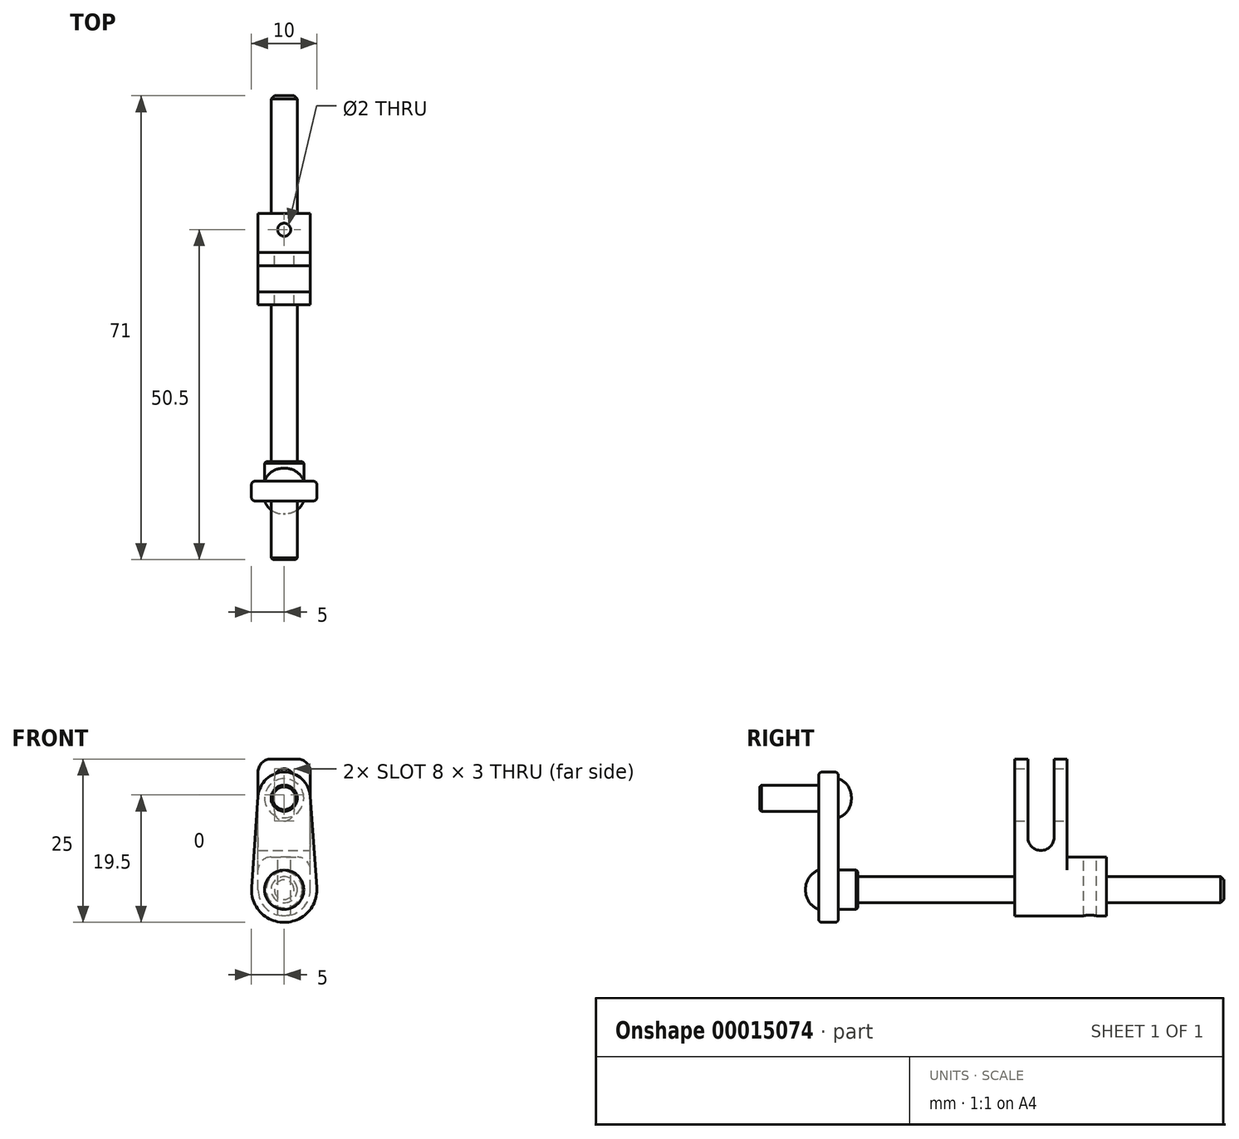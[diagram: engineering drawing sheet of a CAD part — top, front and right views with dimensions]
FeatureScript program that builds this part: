
annotation { "Feature Type Name" : "Feature", "Feature Type Description" : "" }
export const myFeature = defineFeature(function(context is Context, id is Id, definition is map)
    precondition{}
    {
        {
            var Q0;
            Q0=qCreatedBy(makeId("Front.planeOp"),FACE);
            var sketch = newSketch(context, id + "F0", { "sketchPlane" : qUnion([Q0])});
            skCircle(sketch, "E0", {"center": v(0, 0) * mm, "radius": 2 * mm});
            skArc(sketch, "E1", {"start": v(-4.99, 0.36) * mm, "mid": v(0, -5) * mm, "end": v(4.99, 0.36) * mm});
            skCircle(sketch, "E2", {"center": v(0, 14) * mm, "radius": 2 * mm});
            skArc(sketch, "E3", {"start": v(3.99, 14.29) * mm, "mid": v(0, 18) * mm, "end": v(-3.99, 14.29) * mm});
            skLineSegment(sketch, "E4", {"start": v(0, 0) * mm, "end": v(0, 19.62) * mm, "construction": true});
            skLineSegment(sketch, "E5", {"start": v(-3.99, 14.29) * mm, "end": v(-4.99, 0.36) * mm});
            skLineSegment(sketch, "E6", {"start": v(4.99, 0.36) * mm, "end": v(3.99, 14.29) * mm});
            skSolve(sketch);
        }
        {
            var Q0;
            Q0=makeQuery(id+"F0.imprint","IMPRINT",FACE,{"disambiguationData":[TD([[makeQuery(id+"F0.imprint","IMPRINT",EDGE,{"derivedFrom":sQuery(id+"F0.wireOp",EDGE,"E0")}),-1.0]])]});
            extrude(context, id + "F1", {"entities" : qUnion([Q0]), "endBound" : BoundingType.SYMMETRIC, "depth" : 3 * mm});
        }
        {
            var Q0;
            Q0=makeQuery(id+"F1.opExtrude","CAP_EDGE",EDGE,{"disambiguationData":[OSD([sQuery(id+"F0.wireOp",EDGE,"E6")])],"isStart":false});
            var Q1;
            Q1=makeQuery(id+"F1.opExtrude","CAP_EDGE",EDGE,{"disambiguationData":[OSD([sQuery(id+"F0.wireOp",EDGE,"E6")])],"isStart":true});
            fillet(context, id + "F2", {"entities" : qUnion([Q0, Q1]), "radius" : .5 * mm, "tangentPropagation" : true, "allowEdgeOverflow" : false});
        }
        {
            var Q0;
            Q0=makeQuery(id+"F1.opExtrude","CAP_FACE",FACE,{"disambiguationData":[OSD([sQuery(id+"F0.wireOp",EDGE,"E0"),sQuery(id+"F0.wireOp",EDGE,"E1"),sQuery(id+"F0.wireOp",EDGE,"E2"),sQuery(id+"F0.wireOp",EDGE,"E3"),sQuery(id+"F0.wireOp",EDGE,"E5"),sQuery(id+"F0.wireOp",EDGE,"E6")])],"isStart":true});
            var sketch = newSketch(context, id + "F3", { "sketchPlane" : qUnion([Q0])});
            skCircle(sketch, "E7.0", {"center": v(0, 14) * mm, "radius": 2 * mm});
            skSolve(sketch);
        }
        {
            var Q0;
            Q0=makeQuery(id+"F3.imprint","IMPRINT",FACE,{"disambiguationData":[TD([[makeQuery(id+"F3.imprint","IMPRINT",EDGE,{"derivedFrom":sQuery(id+"F3.wireOp",EDGE,"E7.0")}),-1.0]])]});
            extrude(context, id + "F4", {"entities" : qUnion([Q0]), "oppositeDirection" : true, "depth" : 12 * mm});
        }
        {
            var Q0;
            Q0=makeQuery(id+"F4.opExtrude","CAP_FACE",FACE,{"disambiguationData":[OSD([sQuery(id+"F3.wireOp",EDGE,"E7.0")])],"isStart":true});
            var sketch = newSketch(context, id + "F5", { "sketchPlane" : qUnion([Q0])});
            skCircle(sketch, "E8.0.0", {"center": v(0, 14) * mm, "radius": 2 * mm});
            skCircle(sketch, "E9", {"center": v(0, 14) * mm, "radius": 3 * mm});
            skSolve(sketch);
        }
        {
            var Q0;
            Q0=makeQuery(id+"F5.imprint","IMPRINT",FACE,{"disambiguationData":[TD([[makeQuery(id+"F5.imprint","IMPRINT",EDGE,{"derivedFrom":sQuery(id+"F5.wireOp",EDGE,"E8.0.0")}),1.0]])]});
            var Q1;
            Q1=makeQuery(id+"F5.imprint","IMPRINT",FACE,{"disambiguationData":[TD([[makeQuery(id+"F5.imprint","IMPRINT",EDGE,{"derivedFrom":sQuery(id+"F5.wireOp",EDGE,"E8.0.0")}),-1.0]])]});
            extrude(context, id + "F6", {"entities" : qUnion([Q0, Q1]), "operationType" : NewBodyOperationType.ADD, "depth" : 2 * mm});
        }
        {
            var Q0;
            Q0=makeQuery(id+"F6.opExtrude","CAP_EDGE",EDGE,{"disambiguationData":[OSD([sQuery(id+"F5.wireOp",EDGE,"E9")])],"isStart":false});
            fillet(context, id + "F7", {"entities" : qUnion([Q0]), "radius" : 3 * mm, "tangentPropagation" : true, "allowEdgeOverflow" : false});
        }
        {
            var Q0;
            Q0=makeQuery(id+"F4.opExtrude","CAP_EDGE",EDGE,{"disambiguationData":[OSD([sQuery(id+"F3.wireOp",EDGE,"E7.0")])],"isStart":false});
            chamfer(context, id + "F8", {"entities" : qUnion([Q0]), "width" : .25 * mm, "tangentPropagation" : true});
        }
        {
            var Q0;
            Q0=makeQuery(id+"F1.opExtrude","CAP_FACE",FACE,{"disambiguationData":[OSD([sQuery(id+"F0.wireOp",EDGE,"E0"),sQuery(id+"F0.wireOp",EDGE,"E1"),sQuery(id+"F0.wireOp",EDGE,"E2"),sQuery(id+"F0.wireOp",EDGE,"E3"),sQuery(id+"F0.wireOp",EDGE,"E5"),sQuery(id+"F0.wireOp",EDGE,"E6")])],"isStart":true});
            var sketch = newSketch(context, id + "F9", { "sketchPlane" : qUnion([Q0])});
            skCircle(sketch, "E10.0", {"center": v(0, 0) * mm, "radius": 2 * mm});
            skCircle(sketch, "E11", {"center": v(0, 0) * mm, "radius": 3 * mm});
            skSolve(sketch);
        }
        {
            var Q0;
            Q0=makeQuery(id+"F9.imprint","IMPRINT",FACE,{"disambiguationData":[TD([[makeQuery(id+"F9.imprint","IMPRINT",EDGE,{"derivedFrom":sQuery(id+"F9.wireOp",EDGE,"E10.0")}),-1.0]])]});
            var Q1;
            Q1=makeQuery(id+"F1.opExtrude","CAP_FACE",FACE,{"disambiguationData":[OSD([sQuery(id+"F0.wireOp",EDGE,"E0"),sQuery(id+"F0.wireOp",EDGE,"E1"),sQuery(id+"F0.wireOp",EDGE,"E2"),sQuery(id+"F0.wireOp",EDGE,"E3"),sQuery(id+"F0.wireOp",EDGE,"E5"),sQuery(id+"F0.wireOp",EDGE,"E6")])],"isStart":false});
            extrude(context, id + "F10", {"entities" : qUnion([Q0]), "endBound" : BoundingType.UP_TO_SURFACE, "oppositeDirection" : true, "endBoundEntityFace" : qUnion([Q1]), "depth" : 25 * mm});
        }
        {
            var Q0;
            Q0=makeQuery(id+"F10.opExtrude","CAP_FACE",FACE,{"disambiguationData":[OSD([sQuery(id+"F9.wireOp",EDGE,"E10.0")])],"isStart":false});
            var sketch = newSketch(context, id + "F11", { "sketchPlane" : qUnion([Q0])});
            skCircle(sketch, "E12.0", {"center": v(0, 0) * mm, "radius": 2 * mm});
            skCircle(sketch, "E13", {"center": v(0, 0) * mm, "radius": 3 * mm});
            skSolve(sketch);
        }
        {
            var Q0;
            Q0=makeQuery(id+"F11.imprint","IMPRINT",FACE,{"disambiguationData":[TD([[makeQuery(id+"F11.imprint","IMPRINT",EDGE,{"derivedFrom":sQuery(id+"F11.wireOp",EDGE,"E12.0")}),1.0]])]});
            var Q1;
            Q1=makeQuery(id+"F11.imprint","IMPRINT",FACE,{"disambiguationData":[TD([[makeQuery(id+"F11.imprint","IMPRINT",EDGE,{"derivedFrom":sQuery(id+"F11.wireOp",EDGE,"E12.0")}),-1.0]])]});
            extrude(context, id + "F12", {"entities" : qUnion([Q0, Q1]), "operationType" : NewBodyOperationType.ADD, "depth" : 2 * mm});
        }
        {
            var Q0;
            Q0=makeQuery(id+"F12.opExtrude","CAP_EDGE",EDGE,{"disambiguationData":[OSD([sQuery(id+"F11.wireOp",EDGE,"E13")])],"isStart":false});
            fillet(context, id + "F13", {"entities" : qUnion([Q0]), "radius" : 3 * mm, "tangentPropagation" : true, "allowEdgeOverflow" : false});
        }
        {
            var Q0;
            Q0=makeQuery(id+"F9.imprint","IMPRINT",FACE,{"disambiguationData":[TD([[makeQuery(id+"F9.imprint","IMPRINT",EDGE,{"derivedFrom":sQuery(id+"F9.wireOp",EDGE,"E10.0")}),-1.0]])]});
            var Q1;
            Q1=makeQuery(id+"F9.imprint","IMPRINT",FACE,{"disambiguationData":[TD([[makeQuery(id+"F9.imprint","IMPRINT",EDGE,{"derivedFrom":sQuery(id+"F9.wireOp",EDGE,"E10.0")}),1.0]])]});
            extrude(context, id + "F14", {"entities" : qUnion([Q0, Q1]), "operationType" : NewBodyOperationType.ADD, "depth" : 3 * mm});
        }
        {
            var Q0;
            Q0=makeQuery(id+"F14.opExtrude","CAP_FACE",FACE,{"disambiguationData":[OSD([sQuery(id+"F9.wireOp",EDGE,"E11")])],"isStart":false});
            var sketch = newSketch(context, id + "F15", { "sketchPlane" : qUnion([Q0])});
            skCircle(sketch, "E14.0", {"center": v(0, 0) * mm, "radius": 2 * mm});
            skSolve(sketch);
        }
        {
            var Q0;
            Q0=makeQuery(id+"F15.imprint","IMPRINT",FACE,{"disambiguationData":[TD([[makeQuery(id+"F15.imprint","IMPRINT",EDGE,{"derivedFrom":sQuery(id+"F15.wireOp",EDGE,"E14.0")}),1.0]])]});
            extrude(context, id + "F16", {"entities" : qUnion([Q0]), "operationType" : NewBodyOperationType.ADD, "depth" : 56 * mm});
        }
        {
            var Q0;
            Q0=makeQuery(id+"F16.opExtrude","CAP_EDGE",EDGE,{"disambiguationData":[OSD([sQuery(id+"F15.wireOp",EDGE,"E14.0")])],"isStart":false});
            chamfer(context, id + "F17", {"entities" : qUnion([Q0]), "width" : .5 * mm, "tangentPropagation" : true});
        }
        {
            var Q0;
            Q0=makeQuery(id+"F14.opExtrude","CAP_EDGE",EDGE,{"disambiguationData":[OSD([sQuery(id+"F9.wireOp",EDGE,"E11")])],"isStart":false});
            chamfer(context, id + "F18", {"entities" : qUnion([Q0]), "width" : .25 * mm, "tangentPropagation" : true});
        }
        {
            var Q0;
            Q0=makeQuery(id+"F14.opExtrude","CAP_FACE",FACE,{"disambiguationData":[OSD([sQuery(id+"F9.wireOp",EDGE,"E11")])],"isStart":false});
            var Q1;
            Q1=makeQuery(id+"F16.opExtrude","CAP_FACE",FACE,{"disambiguationData":[OSD([sQuery(id+"F15.wireOp",EDGE,"E14.0")])],"isStart":false});
            cPlane(context, id + "F19", {"entities" : qUnion([Q0, Q1]), "cplaneType" : CPlaneType.MID_PLANE, "offset" : 150 * mm, "width" : 150 * mm, "height" : 150 * mm});
        }
        {
            var Q0;
            Q0=qCreatedBy(id+"F19.planeOp",FACE);
            var sketch = newSketch(context, id + "F20", { "sketchPlane" : qUnion([Q0])});
            skCircle(sketch, "E15.0", {"center": v(0, 0) * mm, "radius": 2 * mm});
            skCircle(sketch, "E16", {"center": v(0, 0) * mm, "radius": 4 * mm});
            skLineSegment(sketch, "E17", {"start": v(0, -5.55) * mm, "end": v(0, 19.01) * mm, "construction": true});
            skLineSegment(sketch, "E18.top", {"start": v(-4, 5) * mm, "end": v(4, 5) * mm});
            skLineSegment(sketch, "E18.left", {"start": v(-4, 0) * mm, "end": v(-4, 5) * mm});
            skLineSegment(sketch, "E18.right", {"start": v(4, 0) * mm, "end": v(4, 5) * mm});
            skLineSegment(sketch, "E19.top", {"start": v(-4, 20) * mm, "end": v(4, 20) * mm});
            skLineSegment(sketch, "E19.left", {"start": v(-4, 0) * mm, "end": v(-4, 20) * mm});
            skLineSegment(sketch, "E19.right", {"start": v(4, 0) * mm, "end": v(4, 20) * mm});
            skPoint(sketch, "E20", {"position": v(0, -4) * mm});
            skArc(sketch, "E21", {"start": v(1.5, 17) * mm, "mid": v(0, 18.5) * mm, "end": v(-1.5, 17) * mm});
            skArc(sketch, "E22", {"start": v(-1.5, 12) * mm, "mid": v(0, 10.5) * mm, "end": v(1.5, 12) * mm});
            skLineSegment(sketch, "E23", {"start": v(-1.5, 17) * mm, "end": v(-1.5, 12) * mm});
            skLineSegment(sketch, "E24", {"start": v(1.5, 12) * mm, "end": v(1.5, 17) * mm});
            skSolve(sketch);
        }
        {
            var Q0;
            {var subQ2=sQuery(id+"F20.wireOp",EDGE,"E18.top");Q0=makeQuery(id+"F20.imprint","IMPRINT",FACE,{"disambiguationData":[TD([[makeQuery(id+"F20.imprint","IMPRINT",EDGE,{"derivedFrom":subQ2}),1.0]])]});}
            var Q1;
            {var subQ3=sQuery(id+"F20.wireOp",EDGE,"E18.top");Q1=makeQuery(id+"F20.imprint","IMPRINT",FACE,{"disambiguationData":[TD([[makeQuery(id+"F20.imprint","IMPRINT",EDGE,{"derivedFrom":subQ3}),-1.0]])]});}
            var Q2;
            Q2=makeQuery(id+"F20.imprint","IMPRINT",FACE,{"disambiguationData":[TD([[makeQuery(id+"F20.imprint","IMPRINT",EDGE,{"derivedFrom":sQuery(id+"F20.wireOp",EDGE,"E15.0")}),-1.0]])]});
            extrude(context, id + "F21", {"entities" : qUnion([Q0, Q1, Q2]), "endBound" : BoundingType.SYMMETRIC, "oppositeDirection" : true, "depth" : 8 * mm});
        }
        {
            var Q0;
            {var subQ3=sQuery(id+"F20.wireOp",EDGE,"E18.top");Q0=makeQuery(id+"F20.imprint","IMPRINT",FACE,{"disambiguationData":[TD([[makeQuery(id+"F20.imprint","IMPRINT",EDGE,{"derivedFrom":subQ3}),-1.0]])]});}
            var Q1;
            Q1=makeQuery(id+"F20.imprint","IMPRINT",FACE,{"disambiguationData":[TD([[makeQuery(id+"F20.imprint","IMPRINT",EDGE,{"derivedFrom":sQuery(id+"F20.wireOp",EDGE,"E15.0")}),-1.0]])]});
            extrude(context, id + "F22", {"entities" : qUnion([Q0, Q1]), "operationType" : NewBodyOperationType.ADD, "depth" : (14 - 4) * mm});
        }
        {
            var Q0;
            {var subQ0=sQuery(id+"F20.wireOp",EDGE,"E19.left");Q0=makeQuery(id+"F22.boolean.opBoolean","MERGE",FACE,{"derivedFrom":[makeQuery(id+"F21.opExtrude","SWEPT_FACE",FACE,{"disambiguationData":[OSD([subQ0])]}),makeQuery(id+"F22.opExtrude","SWEPT_FACE",FACE,{"disambiguationData":[OSD([subQ0])]})]});}
            var sketch = newSketch(context, id + "F23", { "sketchPlane" : qUnion([Q0])});
            skLineSegment(sketch, "E25", {"start": v(32.5, 20) * mm, "end": v(32.5, 2.01) * mm, "construction": true});
            skLineSegment(sketch, "E26.rect.bottom", {"start": v(34.5, 20) * mm, "end": v(30.5, 20) * mm});
            skLineSegment(sketch, "E26.rect.top", {"start": v(34.5, 6) * mm, "end": v(30.5, 6) * mm});
            skLineSegment(sketch, "E26.rect.left", {"start": v(34.5, 20) * mm, "end": v(34.5, 6) * mm});
            skLineSegment(sketch, "E26.rect.right", {"start": v(30.5, 20) * mm, "end": v(30.5, 6) * mm});
            skPoint(sketch, "E26.rect.middle", {"position": v(32.5, 13) * mm});
            skSolve(sketch);
        }
        {
            var Q0;
            Q0=makeQuery(id+"F23.imprint","IMPRINT",FACE,{"disambiguationData":[TD([[makeQuery(id+"F23.imprint","IMPRINT",EDGE,{"derivedFrom":sQuery(id+"F23.wireOp",EDGE,"E26.rect.bottom")}),-1.0]])]});
            extrude(context, id + "F24", {"entities" : qUnion([Q0]), "operationType" : NewBodyOperationType.REMOVE, "endBound" : BoundingType.THROUGH_ALL, "oppositeDirection" : true, "depth" : 25 * mm});
        }
        {
            var Q0;
            Q0=makeQuery(id+"F22.opExtrude","SWEPT_FACE",FACE,{"disambiguationData":[OSD([sQuery(id+"F20.wireOp",EDGE,"E18.top")])]});
            var sketch = newSketch(context, id + "F25", { "sketchPlane" : qUnion([Q0])});
            skLineSegment(sketch, "E27", {"start": v(0, 36.5) * mm, "end": v(0, 42.5) * mm, "construction": true});
            skCircle(sketch, "E28", {"center": v(0, 40) * mm, "radius": 1 * mm});
            skSolve(sketch);
        }
        {
            var Q0;
            Q0=makeQuery(id+"F25.imprint","IMPRINT",FACE,{"disambiguationData":[TD([[makeQuery(id+"F25.imprint","IMPRINT",EDGE,{"derivedFrom":sQuery(id+"F25.wireOp",EDGE,"E28")}),1.0]])]});
            var Q1;
            Q1=sQuery(id+"F25.wireOp",EDGE,"E28");
            extrude(context, id + "F26", {"entities" : qUnion([Q0]), "operationType" : NewBodyOperationType.REMOVE, "surfaceEntities" : qUnion([Q1]), "endBound" : BoundingType.UP_TO_NEXT, "oppositeDirection" : true, "depth" : 25 * mm});
        }
        {
            var Q0;
            Q0=makeQuery(id+"F22.opExtrude","SWEPT_EDGE",EDGE,{"disambiguationData":[OSD([sQuery(id+"F20.wireOp",EDGE,"E18.top"),sQuery(id+"F20.wireOp",EDGE,"E19.left")])]});
            var Q1;
            Q1=makeQuery(id+"F22.opExtrude","SWEPT_EDGE",EDGE,{"disambiguationData":[OSD([sQuery(id+"F20.wireOp",EDGE,"E18.top"),sQuery(id+"F20.wireOp",EDGE,"E19.right")])]});
            var Q2;
            {var subQ0=sQuery(id+"F20.wireOp",EDGE,"E19.top");var subQ1=sQuery(id+"F20.wireOp",EDGE,"E19.left");Q2=makeQuery(id+"F24.boolean.opBoolean","SPLIT",EDGE,{"disambiguationData":[TD([makeQuery(id+"F24.opExtrude","SWEPT_FACE",FACE,{"disambiguationData":[OSD([sQuery(id+"F23.wireOp",EDGE,"E26.rect.left")])]})])],"derivedFrom":makeQuery(id+"F21.opExtrude","SWEPT_EDGE",EDGE,{"disambiguationData":[OSD([subQ0,subQ1])]})});}
            var Q3;
            {var subQ0=sQuery(id+"F20.wireOp",EDGE,"E19.top");var subQ1=sQuery(id+"F20.wireOp",EDGE,"E19.right");Q3=makeQuery(id+"F24.boolean.opBoolean","SPLIT",EDGE,{"disambiguationData":[TD([makeQuery(id+"F24.opExtrude","SWEPT_FACE",FACE,{"disambiguationData":[OSD([sQuery(id+"F23.wireOp",EDGE,"E26.rect.left")])]})])],"derivedFrom":makeQuery(id+"F21.opExtrude","SWEPT_EDGE",EDGE,{"disambiguationData":[OSD([subQ0,subQ1])]})});}
            var Q4;
            {var subQ0=sQuery(id+"F20.wireOp",EDGE,"E19.top");var subQ1=sQuery(id+"F20.wireOp",EDGE,"E19.right");Q4=makeQuery(id+"F24.boolean.opBoolean","SPLIT",EDGE,{"disambiguationData":[TD([makeQuery(id+"F24.opExtrude","SWEPT_FACE",FACE,{"disambiguationData":[OSD([sQuery(id+"F23.wireOp",EDGE,"E26.rect.right")])]})])],"derivedFrom":makeQuery(id+"F21.opExtrude","SWEPT_EDGE",EDGE,{"disambiguationData":[OSD([subQ0,subQ1])]})});}
            var Q5;
            {var subQ0=sQuery(id+"F20.wireOp",EDGE,"E19.top");var subQ1=sQuery(id+"F20.wireOp",EDGE,"E19.left");Q5=makeQuery(id+"F24.boolean.opBoolean","SPLIT",EDGE,{"disambiguationData":[TD([makeQuery(id+"F24.opExtrude","SWEPT_FACE",FACE,{"disambiguationData":[OSD([sQuery(id+"F23.wireOp",EDGE,"E26.rect.right")])]})])],"derivedFrom":makeQuery(id+"F21.opExtrude","SWEPT_EDGE",EDGE,{"disambiguationData":[OSD([subQ0,subQ1])]})});}
            var Q6;
            Q6=makeQuery(id+"F24.boolean.opBoolean","COPY",EDGE,{"derivedFrom":makeQuery(id+"F24.opExtrude","SWEPT_EDGE",EDGE,{"disambiguationData":[OSD([sQuery(id+"F23.wireOp",EDGE,"E26.rect.top"),sQuery(id+"F23.wireOp",EDGE,"E26.rect.right")])]})});
            var Q7;
            Q7=makeQuery(id+"F24.boolean.opBoolean","COPY",EDGE,{"derivedFrom":makeQuery(id+"F24.opExtrude","SWEPT_EDGE",EDGE,{"disambiguationData":[OSD([sQuery(id+"F23.wireOp",EDGE,"E26.rect.top"),sQuery(id+"F23.wireOp",EDGE,"E26.rect.left")])]})});
            fillet(context, id + "F27", {"entities" : qUnion([Q0, Q1, Q2, Q3, Q4, Q5, Q6, Q7]), "radius" : 2 * mm, "tangentPropagation" : true, "allowEdgeOverflow" : false});
        }
    });
